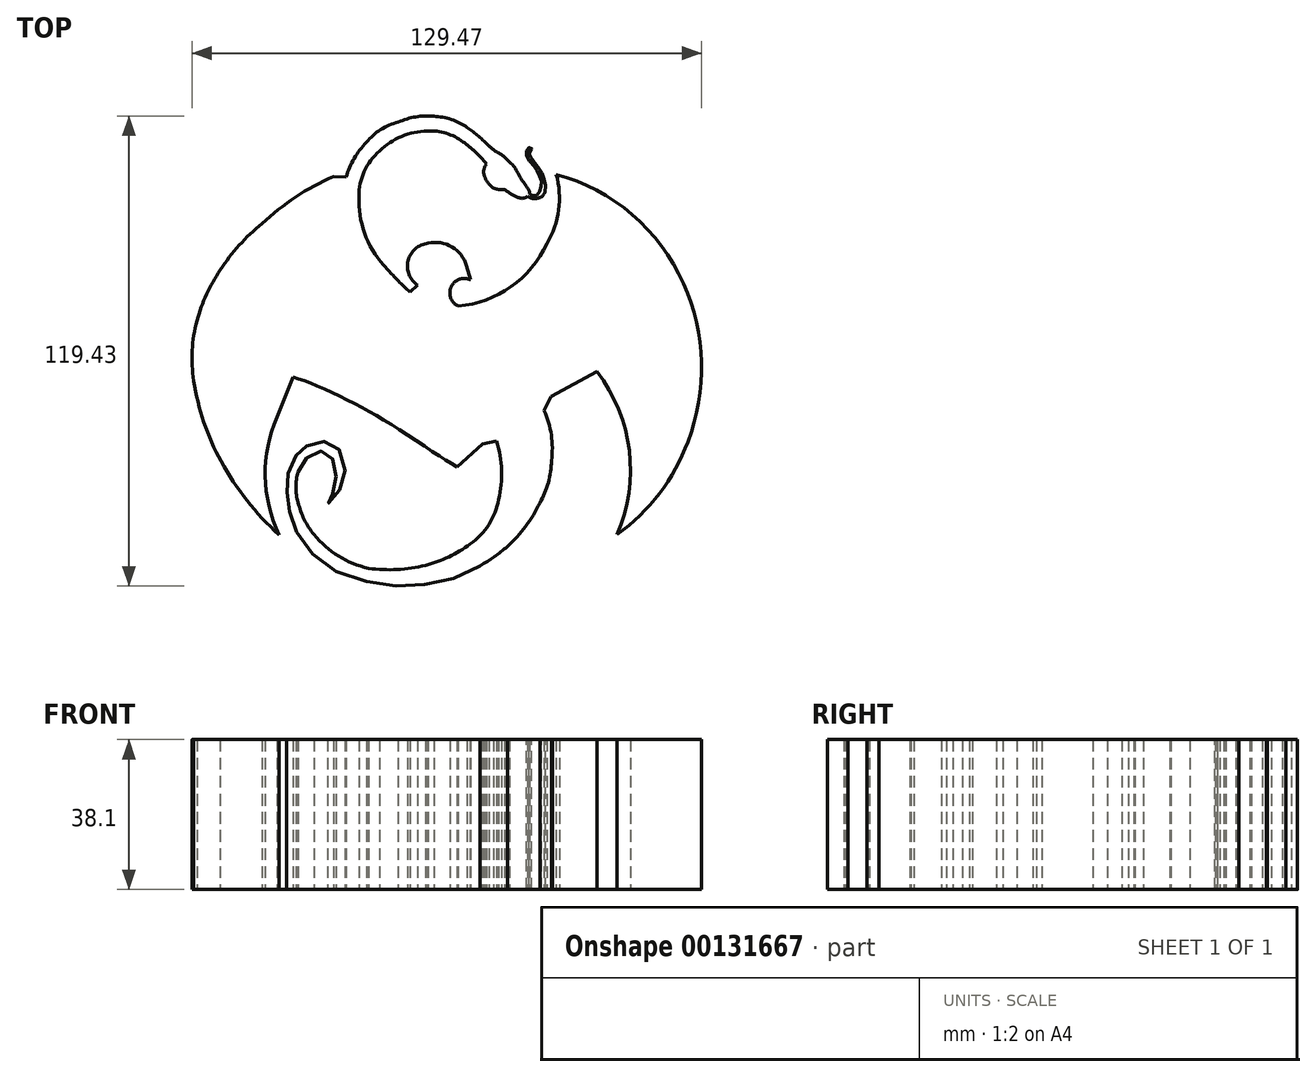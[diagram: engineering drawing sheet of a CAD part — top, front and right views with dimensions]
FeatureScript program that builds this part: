
annotation { "Feature Type Name" : "Feature", "Feature Type Description" : "" }
export const myFeature = defineFeature(function(context is Context, id is Id, definition is map)
    precondition{}
    {
        {
            var Q0;
            Q0=qCreatedBy(makeId("Top.planeOp"),FACE);
            var sketch = newSketch(context, id + "F0", { "sketchPlane" : qUnion([Q0])});
            skCircle(sketch, "E0", {"center": v(0, 0) * mm, "radius": 71.9 * mm});
            skSolve(sketch);
        }
        {
            var Q0;
            Q0=makeQuery(id+"F0.imprint","IMPRINT",FACE,{"disambiguationData":[TD([[makeQuery(id+"F0.imprint","IMPRINT",EDGE,{"derivedFrom":sQuery(id+"F0.wireOp",EDGE,"E0")}),1.0]])]});
            var sketch = newSketch(context, id + "F1", { "sketchPlane" : qUnion([Q0])});
            skArc(sketch, "E1", {"start": v(60.66, 20.92) * mm, "mid": v(47.66, 38.45) * mm, "end": v(28.35, 48.61) * mm});
            skArc(sketch, "E2", {"start": v(61.82, -19.3) * mm, "mid": v(65.25, 0.92) * mm, "end": v(60.66, 20.92) * mm});
            skArc(sketch, "E3", {"start": v(43.85, -42.88) * mm, "mid": v(54.58, -32.42) * mm, "end": v(61.82, -19.3) * mm});
            skArc(sketch, "E4", {"start": v(43.85, -42.88) * mm, "mid": v(46.92, -21.5) * mm, "end": v(38.74, -1.5) * mm});
            skLineSegment(sketch, "E5", {"start": v(38.74, -1.5) * mm, "end": v(27.03, -7.76) * mm});
            skArc(sketch, "E6", {"start": v(27.03, -7.76) * mm, "mid": v(19.36, 0.48) * mm, "end": v(10.88, 7.9) * mm});
            skArc(sketch, "E7", {"start": v(-6.84, 20.47) * mm, "mid": v(1.73, 13.76) * mm, "end": v(10.88, 7.9) * mm});
            skArc(sketch, "E8", {"start": v(-4.19, 31.12) * mm, "mid": v(-9.27, 26.73) * mm, "end": v(-6.84, 20.47) * mm});
            skArc(sketch, "E9", {"start": v(5.6, 25.37) * mm, "mid": v(1.87, 30.22) * mm, "end": v(-4.19, 31.12) * mm});
            skLineSegment(sketch, "E10", {"start": v(5.6, 25.37) * mm, "end": v(6.59, 21.85) * mm});
            skArc(sketch, "E11", {"start": v(6.59, 21.85) * mm, "mid": v(1.67, 20.07) * mm, "end": v(3.46, 15.15) * mm});
            skArc(sketch, "E12", {"start": v(3.46, 15.15) * mm, "mid": v(16.88, 20.07) * mm, "end": v(26, 31.08) * mm});
            skArc(sketch, "E13", {"start": v(26, 31.08) * mm, "mid": v(28.96, 39.6) * mm, "end": v(28.35, 48.61) * mm});
            skFitSpline(sketch, "E14", {"points": [v(21.6, 43.79) * mm, v(22.1, 43.35) * mm, v(23.17, 43.27) * mm, v(23.82, 43.76) * mm, v(24.4, 44.77) * mm, v(24.6, 46.41) * mm, v(24.31, 47.9) * mm, v(23.4, 49.6) * mm, v(22.5, 50.95) * mm, v(21.1, 52.72) * mm, v(20.78, 54.3) * mm, v(21.2, 55.19) * mm, v(21.7, 55.52) * mm, v(22.1, 55.24) * mm, v(22, 54.85) * mm, v(21.57, 54.45) * mm, v(21.56, 53.68) * mm, v(21.82, 53.13) * mm, v(22.21, 52.51) * mm, v(22.94, 51.6) * mm, v(23.72, 50.49) * mm, v(24.34, 49.6) * mm, v(25.2, 47.84) * mm, v(25.6, 45.5) * mm, v(25.24, 43.57) * mm, v(23.67, 42.56) * mm, v(21.87, 42.64) * mm, v(21.06, 43.06) * mm], "startDerivative": vector(14.58, -19.81) * mm, "endDerivative": vector(-21.8, 13.44) * mm});
            skFitSpline(sketch, "E15", {"points": [v(25.3, 43.69) * mm, v(25.48, 44.16) * mm], "startDerivative": vector(0.15, 0.4) * mm, "endDerivative": vector(0.15, 0.4) * mm});
            skFitSpline(sketch, "E16", {"points": [v(21.6, 43.79) * mm, v(21.48, 44.46) * mm, v(20.86, 45.46) * mm, v(19.47, 47.53) * mm, v(18, 50.13) * mm, v(16.54, 51.79) * mm], "startDerivative": vector(-0.4, 4.44) * mm, "endDerivative": vector(-9.56, 9.23) * mm});
            skFitSpline(sketch, "E17", {"points": [v(16.54, 51.79) * mm, v(14.14, 53.84) * mm, v(12.92, 54.55) * mm, v(11.33, 55.8) * mm], "startDerivative": vector(-5.96, 6.17) * mm, "endDerivative": vector(-4.28, 3.48) * mm});
            skArc(sketch, "E18", {"start": v(11.33, 55.8) * mm, "mid": v(8.66, 58.3) * mm, "end": v(5.74, 60.52) * mm});
            skArc(sketch, "E19", {"start": v(5.74, 60.52) * mm, "mid": v(1.71, 62.58) * mm, "end": v(-2.74, 63.4) * mm});
            skArc(sketch, "E20", {"start": v(-2.74, 63.4) * mm, "mid": v(-7.34, 63.23) * mm, "end": v(-11.76, 61.92) * mm});
            skArc(sketch, "E21", {"start": v(-11.76, 61.92) * mm, "mid": v(-16.22, 60) * mm, "end": v(-19.85, 56.79) * mm});
            skArc(sketch, "E22", {"start": v(-19.85, 56.79) * mm, "mid": v(-22.97, 52.68) * mm, "end": v(-24.99, 47.92) * mm});
            skArc(sketch, "E23", {"start": v(-24.99, 47.92) * mm, "mid": v(-26.18, 41.9) * mm, "end": v(-26, 35.75) * mm});
            skArc(sketch, "E24", {"start": v(-26, 35.75) * mm, "mid": v(-23.87, 27.47) * mm, "end": v(-19.6, 20.07) * mm});
            skPoint(sketch, "E24.endSnap0", {"position": v(16.88, 20.07) * mm});
            skArc(sketch, "E25", {"start": v(-19.6, 20.07) * mm, "mid": v(-13.83, 13.28) * mm, "end": v(-6.87, 7.7) * mm});
            skArc(sketch, "E26", {"start": v(5, -4.45) * mm, "mid": v(-0.5, 2.06) * mm, "end": v(-6.87, 7.7) * mm});
            skArc(sketch, "E27", {"start": v(13.23, -19.15) * mm, "mid": v(9.6, -11.53) * mm, "end": v(5, -4.45) * mm});
            skArc(sketch, "E28", {"start": v(13.71, -33.95) * mm, "mid": v(14.5, -26.51) * mm, "end": v(13.23, -19.15) * mm});
            skArc(sketch, "E29", {"start": v(6.49, -45.26) * mm, "mid": v(11.26, -40.34) * mm, "end": v(13.71, -33.95) * mm});
            skArc(sketch, "E30", {"start": v(-4.84, -50.7) * mm, "mid": v(1.08, -48.53) * mm, "end": v(6.49, -45.26) * mm});
            skArc(sketch, "E31", {"start": v(-19.3, -51.45) * mm, "mid": v(-12.03, -51.77) * mm, "end": v(-4.84, -50.7) * mm});
            skArc(sketch, "E32", {"start": v(-33.14, -42.88) * mm, "mid": v(-26.96, -48.37) * mm, "end": v(-19.3, -51.45) * mm});
            skArc(sketch, "E33", {"start": v(-37.18, -34.75) * mm, "mid": v(-35.66, -39.06) * mm, "end": v(-33.14, -42.88) * mm});
            skArc(sketch, "E34", {"start": v(-37.18, -26.97) * mm, "mid": v(-37.77, -30.86) * mm, "end": v(-37.18, -34.75) * mm});
            skFitSpline(sketch, "E35", {"points": [v(-37.18, -26.97) * mm, v(-36.42, -25.05) * mm, v(-34.68, -23.2) * mm, v(-32.86, -22.06) * mm, v(-30.68, -21.75) * mm, v(-29.15, -22.69) * mm, v(-28.24, -24.09) * mm, v(-27.64, -26.6) * mm, v(-27.64, -29.98) * mm, v(-28.32, -32.19) * mm, v(-29.28, -34.34) * mm, v(-29.77, -35.02) * mm, v(-29, -34.58) * mm, v(-27.3, -32.63) * mm, v(-25.9, -30.06) * mm, v(-25.23, -26.37) * mm, v(-26.09, -22.27) * mm, v(-28.47, -19.88) * mm, v(-30.5, -19.24) * mm, v(-33.41, -19.46) * mm, v(-35.57, -20.66) * mm, v(-36.55, -21.35) * mm, v(-38.2, -23.53) * mm, v(-39.54, -26.57) * mm, v(-40.05, -29.56) * mm, v(-40.05, -32.55) * mm, v(-39.69, -35.49) * mm, v(-38.82, -38.9) * mm, v(-37.18, -42.88) * mm, v(-33.26, -48.02) * mm, v(-27.46, -52.27) * mm, v(-19.08, -55) * mm, v(-11.67, -55.95) * mm, v(-4.91, -55.58) * mm, v(2.5, -53.96) * mm, v(9.04, -50.8) * mm], "startDerivative": vector(24.97, 86.44) * mm, "endDerivative": vector(149.13, 82.75) * mm});
            skArc(sketch, "E36", {"start": v(9.04, -50.8) * mm, "mid": v(12.62, -48.52) * mm, "end": v(15.96, -45.88) * mm});
            skArc(sketch, "E37", {"start": v(15.96, -45.88) * mm, "mid": v(20.6, -40.78) * mm, "end": v(24.19, -34.88) * mm});
            skArc(sketch, "E38", {"start": v(24.19, -34.88) * mm, "mid": v(26.36, -29.67) * mm, "end": v(27.15, -24.08) * mm});
            skArc(sketch, "E39", {"start": v(27.15, -24.08) * mm, "mid": v(27.12, -17.6) * mm, "end": v(25.27, -11.4) * mm});
            skArc(sketch, "E40", {"start": v(25.27, -11.4) * mm, "mid": v(22.2, -5.52) * mm, "end": v(17.43, -0.9) * mm});
            skFitSpline(sketch, "E41", {"points": [v(17.43, -0.9) * mm, v(12.98, 3.16) * mm, v(6.64, 7.68) * mm, v(-3.83, 14.94) * mm, v(-8.83, 18.8) * mm, v(-12.63, 22.45) * mm, v(-15.5, 25.6) * mm], "startDerivative": vector(-27.5, 26.61) * mm, "endDerivative": vector(-20.85, 23.44) * mm});
            skArc(sketch, "E42", {"start": v(-21.74, 43.03) * mm, "mid": v(-20.33, 33.7) * mm, "end": v(-15.5, 25.6) * mm});
            skArc(sketch, "E43", {"start": v(-16.49, 54.57) * mm, "mid": v(-20.4, 49.4) * mm, "end": v(-21.74, 43.03) * mm});
            skArc(sketch, "E44", {"start": v(-4.38, 59.64) * mm, "mid": v(-10.92, 58.27) * mm, "end": v(-16.49, 54.57) * mm});
            skArc(sketch, "E45", {"start": v(4.73, 56.88) * mm, "mid": v(0.42, 59.07) * mm, "end": v(-4.38, 59.64) * mm});
            skFitSpline(sketch, "E46", {"points": [v(4.73, 56.88) * mm, v(6.75, 55.31) * mm, v(8.6, 53.62) * mm, v(10.7, 51.31) * mm], "startDerivative": vector(6.38, -4.8) * mm, "endDerivative": vector(5.95, -6.77) * mm});
            skArc(sketch, "E47", {"start": v(10.7, 51.31) * mm, "mid": v(9.96, 49.6) * mm, "end": v(10.3, 47.77) * mm});
            skArc(sketch, "E48", {"start": v(10.3, 47.77) * mm, "mid": v(11.15, 46.33) * mm, "end": v(12.4, 45.22) * mm});
            skArc(sketch, "E49", {"start": v(12.4, 45.22) * mm, "mid": v(13.76, 44.77) * mm, "end": v(15.2, 44.76) * mm});
            skFitSpline(sketch, "E50", {"points": [v(15.2, 44.76) * mm, v(16.45, 43.96) * mm, v(17.5, 43.27) * mm, v(18.7, 42.78) * mm, v(19.79, 42.55) * mm, v(21.06, 43.06) * mm], "startDerivative": vector(6.07, -3.77) * mm, "endDerivative": vector(6.32, 3.49) * mm});
            skArc(sketch, "E51", {"start": v(-28.21, 48.14) * mm, "mid": v(-37.82, 42.87) * mm, "end": v(-46.42, 36.08) * mm});
            skArc(sketch, "E52", {"start": v(-46.42, 36.08) * mm, "mid": v(-52.17, 30.64) * mm, "end": v(-57, 24.35) * mm});
            skArc(sketch, "E53", {"start": v(-57, 24.35) * mm, "mid": v(-60.46, 18.17) * mm, "end": v(-62.86, 11.5) * mm});
            skArc(sketch, "E54", {"start": v(-62.86, 11.5) * mm, "mid": v(-64.14, 3.9) * mm, "end": v(-63.71, -3.8) * mm});
            skArc(sketch, "E55", {"start": v(-63.71, -3.8) * mm, "mid": v(-61.16, -14.34) * mm, "end": v(-56.78, -24.25) * mm});
            skArc(sketch, "E56", {"start": v(-56.78, -24.25) * mm, "mid": v(-50.2, -34.2) * mm, "end": v(-42.07, -42.93) * mm});
            skArc(sketch, "E57", {"start": v(-42.62, -13.05) * mm, "mid": v(-45.56, -28.05) * mm, "end": v(-42.07, -42.93) * mm});
            skFitSpline(sketch, "E58", {"points": [v(-42.62, -13.05) * mm, v(-38.55, -2.88) * mm], "startDerivative": vector(4.06, 10.18) * mm, "endDerivative": vector(4.06, 10.18) * mm});
            skFitSpline(sketch, "E59", {"points": [v(-38.55, -2.88) * mm, v(-34.11, -4.36) * mm, v(-27.18, -7.5) * mm, v(-19.59, -11.39) * mm, v(-11.63, -16.1) * mm, v(-2.01, -22.49) * mm, v(3.17, -25.73) * mm], "startDerivative": vector(32.67, -9.83) * mm, "endDerivative": vector(32.07, -19.47) * mm});
            skFitSpline(sketch, "E60", {"points": [v(3.17, -25.73) * mm, v(9.65, -19.9) * mm], "startDerivative": vector(6.48, 5.83) * mm, "endDerivative": vector(6.48, 5.83) * mm});
            skArc(sketch, "E61", {"start": v(-28.21, 48.14) * mm, "mid": v(-29.5, 35.87) * mm, "end": v(-26.3, 23.96) * mm});
            skArc(sketch, "E62", {"start": v(-26.3, 23.96) * mm, "mid": v(-19.39, 14.18) * mm, "end": v(-10.49, 6.17) * mm});
            skFitSpline(sketch, "E63", {"points": [v(-10.49, 6.17) * mm, v(-5.18, 1.56) * mm, v(-0.9, -2.89) * mm, v(3.56, -8.5) * mm, v(6.69, -14.6) * mm, v(9.65, -19.9) * mm], "startDerivative": vector(26.86, -22.45) * mm, "endDerivative": vector(15.9, -27.04) * mm});
            skLineSegment(sketch, "E64", {"start": v(27.03, -7.76) * mm, "end": v(25.27, -11.4) * mm});
            skLineSegment(sketch, "E65", {"start": v(-6.84, 20.47) * mm, "end": v(-8.83, 18.8) * mm});
            skLineSegment(sketch, "E66", {"start": v(-28.21, 48.14) * mm, "end": v(-24.99, 47.92) * mm});
            skLineSegment(sketch, "E67", {"start": v(9.65, -19.9) * mm, "end": v(13.23, -19.15) * mm});
            skLineSegment(sketch, "E68", {"start": v(21.73, 43.6) * mm, "end": v(21.06, 43.06) * mm});
            skSolve(sketch);
        }
        {
            var Q0;
            Q0 = qSketchRegion(id + "F1", true);
            extrude(context, id + "F2", {"entities" : qUnion([Q0]), "depth" : 38.1 * mm});
        }
    });
